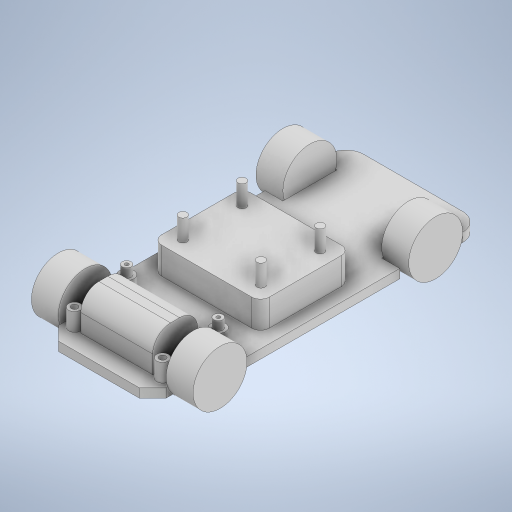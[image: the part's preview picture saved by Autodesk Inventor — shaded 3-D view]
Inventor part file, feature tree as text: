
AUTODESK INVENTOR PART (.ipt)
format: ipt  version: 2024.2 (Build 282272000, 272)  size: 458,752 bytes
history: native  units: mm
features: extrude x11, sketch x11, projected_geometry x5, fillet x2, mirror x2, plane x1
ambient origin geometry x8: Origin, YZ Plane, XZ Plane, XY Plane, X Axis, Y Axis, Z Axis, Center Point
bodies: Body1 (feature_tree)
feature tree (32):
  extrude  "Extrusion5"  Depth=175.0mm
  extrude  "Extrusion6"  Depth=15.0mm
  extrude  "Extrusion7"  Depth=15.0mm
  fillet  "Fillet2"  Radius=10.0mm
  extrude  "Extrusion8"  Depth=10.0mm
  plane  "Work Plane1"
  mirror  "Mirror1"
  extrude  "Extrusion9"  Depth=15.0mm
  mirror  "Mirror2"
  fillet  "Fillet3"  Radius=30.0mm
  extrude  "Extrusion10"  Depth=60.0mm
  extrude  "Extrusion11"  Depth=7.5mm
  extrude  "Extrusion12"  Depth=15.0mm TaperAngle=0.0deg
  extrude  "Extrusion13"  Depth=40.0mm
  extrude  "Extrusion14"  Depth=10.0mm
  extrude  "Extrusion15"  Depth=10.0mm
  sketch  "Sketch6"  dims[d30=75.0mm d31=175.0mm]
  sketch  "Sketch7"  dims[d32=15.0mm d33=15.0mm]
  sketch  "Sketch8"  dims[d34=15.0mm d35=15.0mm d36=10.0mm]
  sketch  "Sketch9"  dims[d37=40.0mm d38=10.0mm]
  sketch  "Sketch10"  dims[d39=10.0mm d40=15.0mm d41=30.0mm]
  sketch  "Sketch12"  dims[d42=5.0mm d43=0.0mm d44=60.0mm]
  sketch  "Sketch14"  dims[d45=50.0mm d46=7.5mm]
  sketch  "Sketch15"  dims[d47=20.0mm d48=15.0mm d49=0.0mm]
  projected_geometry  "Projected Loop1"
  projected_geometry  "Projected Loop2"
  projected_geometry  "Projected Loop3"
  sketch  "Sketch16"  dims[d50=25.0mm d51=40.0mm]
  sketch  "Sketch18"  dims[d52=10.0mm d53=10.0mm]
  projected_geometry  "Projected Loop4"
  projected_geometry  "Projected Loop5"
  sketch  "Sketch19"  dims[d54=20.0mm d55=0.0mm d56=10.0mm d57=30.0mm d58=15.0mm d59=10.0mm d63=15.0mm d64=0.0mm d65=-37.5mm d66=30.0mm d67=15.0mm d68=10.0mm d69=15.0mm d70=0.0mm d71=5.0mm d72=4.5mm d73=4.5mm d74=4.5mm d75=4.5mm d76=43.5mm d77=33.0mm d78=8.5mm d79=8.25mm d80=12.0mm d81=0.0mm d82=51.0mm d83=12.0mm d84=1.0mm d85=8.0mm d86=8.0mm d87=49.0mm d88=1.0mm d89=6.5mm d90=6.5mm d91=30.0mm d92=5.0mm d93=0.0mm d94=5.0mm d95=5.0mm d96=3.5mm d97=3.5mm d98=5.0mm d99=0.0mm d100=5.0mm d101=5.0mm d102=5.0mm d103=0.0mm d104=2.0mm d105=2.0mm d106=0.0mm d107=0.0mm d108=3.5mm d109=3.5mm d110=8.0mm d111=0.0mm]
